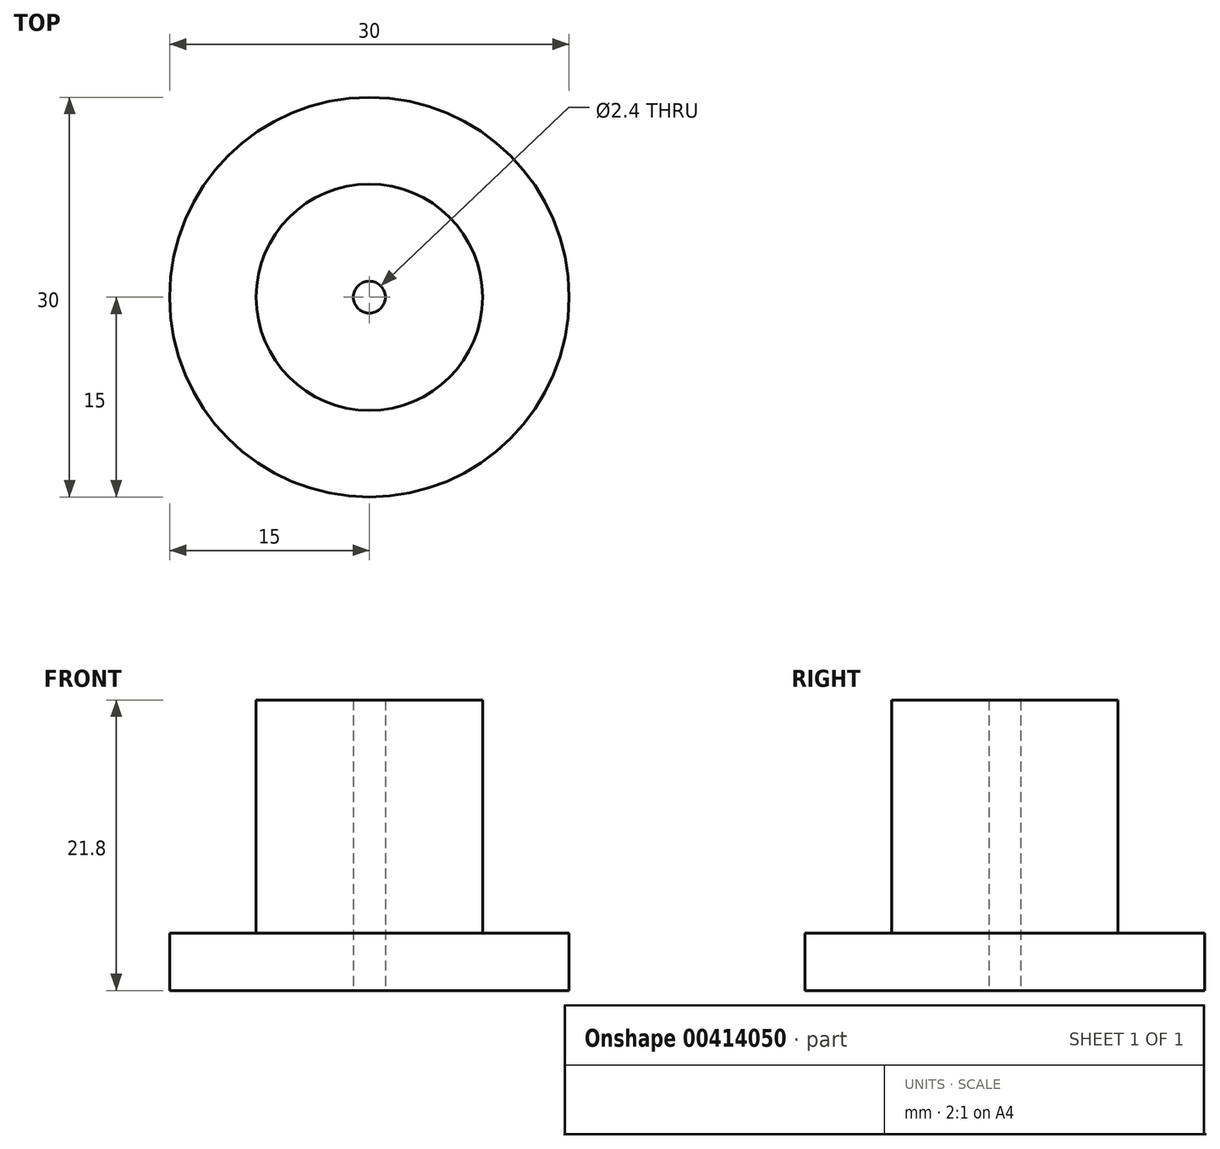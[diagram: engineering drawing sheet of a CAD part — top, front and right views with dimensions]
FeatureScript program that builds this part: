
annotation { "Feature Type Name" : "Feature", "Feature Type Description" : "" }
export const myFeature = defineFeature(function(context is Context, id is Id, definition is map)
    precondition{}
    {
        {
            var Q0;
            Q0=qCreatedBy(makeId("Top.planeOp"),FACE);
            var sketch = newSketch(context, id + "F0", { "sketchPlane" : qUnion([Q0])});
            skCircle(sketch, "E0", {"center": v(0, 0) * mm, "radius": 15 * mm});
            skSolve(sketch);
        }
        {
            var Q0;
            Q0=makeQuery(id+"F0.imprint","IMPRINT",FACE,{"disambiguationData":[TD([[makeQuery(id+"F0.imprint","IMPRINT",EDGE,{"derivedFrom":sQuery(id+"F0.wireOp",EDGE,"E0")}),1.0]])]});
            extrude(context, id + "F1", {"entities" : qUnion([Q0]), "depth" : 21.8 * mm});
        }
        {
            var Q0;
            Q0=makeQuery(id+"F1.opExtrude","CAP_FACE",FACE,{"disambiguationData":[OSD([sQuery(id+"F0.wireOp",EDGE,"E0")])],"isStart":false});
            var sketch = newSketch(context, id + "F2", { "sketchPlane" : qUnion([Q0])});
            skLineSegment(sketch, "E1", {"start": v(0, 15) * mm, "end": v(0, -15) * mm});
            skLineSegment(sketch, "E2", {"start": v(0, -15) * mm, "end": v(0, -8.5) * mm});
            skLineSegment(sketch, "E3", {"start": v(0, 15) * mm, "end": v(0, 8.5) * mm});
            skCircle(sketch, "E4", {"center": v(0, 0) * mm, "radius": 8.5 * mm});
            skSolve(sketch);
        }
        {
            var Q0;
            {var subQ0=sQuery(id+"F2.wireOp",EDGE,"E1");Q0=makeQuery(id+"F2.imprint","IMPRINT",FACE,{"disambiguationData":[TD([[makeQuery(id+"F2.imprint","IMPRINT",EDGE,{"derivedFrom":subQ0}),-1.0]])]});}
            var Q1;
            {var subQ0=sQuery(id+"F2.wireOp",EDGE,"E1");Q1=makeQuery(id+"F2.imprint","IMPRINT",FACE,{"disambiguationData":[TD([[makeQuery(id+"F2.imprint","IMPRINT",EDGE,{"derivedFrom":subQ0}),1.0]])]});}
            extrude(context, id + "F3", {"entities" : qUnion([Q0, Q1]), "operationType" : NewBodyOperationType.REMOVE, "oppositeDirection" : true, "depth" : 17.5 * mm});
        }
        {
            var Q0;
            Q0=makeQuery(id+"F1.opExtrude","CAP_FACE",FACE,{"disambiguationData":[OSD([sQuery(id+"F0.wireOp",EDGE,"E0")])],"isStart":true});
            var sketch = newSketch(context, id + "F4", { "sketchPlane" : qUnion([Q0])});
            skCircle(sketch, "E5", {"center": v(0, 0) * mm, "radius": 1.2 * mm});
            skSolve(sketch);
        }
        {
            var Q0;
            Q0=makeQuery(id+"F4.imprint","IMPRINT",FACE,{"disambiguationData":[TD([[makeQuery(id+"F4.imprint","IMPRINT",EDGE,{"derivedFrom":sQuery(id+"F4.wireOp",EDGE,"E5")}),1.0]])]});
            extrude(context, id + "F5", {"entities" : qUnion([Q0]), "operationType" : NewBodyOperationType.REMOVE, "oppositeDirection" : true, "depth" : 25.4 * mm});
        }
    });
